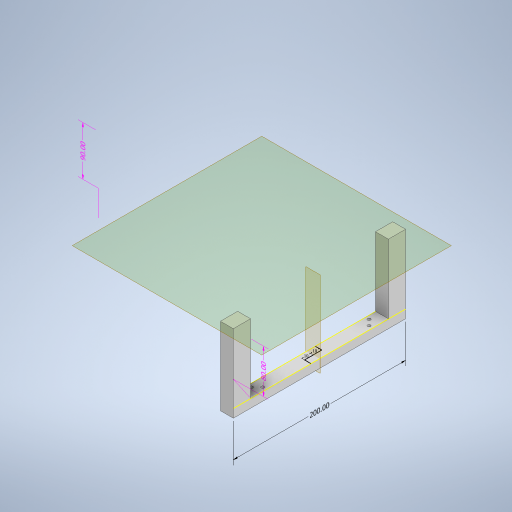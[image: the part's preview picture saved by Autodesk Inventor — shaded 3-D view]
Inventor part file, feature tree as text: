
AUTODESK INVENTOR PART (.ipt)
format: ipt  version: 2023 (Build 270158000, 158)  size: 368,128 bytes
history: native  units: mm
features: sketch x8, other x5, extrude x5, hole x2, plane x2, split x1
ambient origin geometry x8: Origin, YZ Plane, XZ Plane, XY Plane, X Axis, Y Axis, Z Axis, Center Point
bodies: Body1 (feature_tree)
feature tree (23):
  other  "Sólido1"
  other  "Anotaciones"
  extrude  "Extrusión1"  Depth=200.0mm
  hole  "Agujero1"  [1 undecoded]
  extrude  "Extrusión2"  Depth=15.0mm
  extrude  "Extrusión3"  Depth=80.0mm TaperAngle=0.0deg
  extrude  "Extrusión4"  Depth=200.0mm
  extrude  "Extrusión5"  Depth=20.0mm
  hole  "Agujero2"  [1 undecoded]
  plane  "Plano de trabajo1"
  split  "Dividir1"
  plane  "Plano de trabajo2"
  sketch  "Boceto9"  dims[d37=20.0mm d38=20.0mm d39=90.0mm d40=0.0mm d42=10.0mm d43=30.0mm d44=0.0mm d46=1.75mm d47=1.75mm d48=1.75mm d49=1.75mm d50=10.0mm d51=10.0mm d52=15.0mm d56=3.5mm d57=6.0mm d58=4.0mm d59=2.0mm d60=90.0deg d61=8.0mm d62=20.594885mm d63=10.0mm d65=10.0mm d66=10.0mm d67=31.75mm d70=15.0mm d74=200.0mm d78=20.0mm d82=90.0deg d86=10.0mm d87=10.0mm d75=1.454734mm d76=6.982969mm d77=80.0mm d79=4.097996mm d80=1.406125mm d81=90.0mm d83=1.657181mm d84=1.253427mm d85=200.0mm]
  sketch  "Boceto2"  dims[d7=15.0mm d8=200.0mm]
  sketch  "Boceto3"  dims[d9=10.0mm d10=0.0mm]
  sketch  "Boceto4"  dims[d12=1.75mm d13=1.75mm d14=1.75mm d15=1.75mm d16=10.0mm d17=10.0mm d19=30.0mm]
  sketch  "Boceto5"  dims[d20=3.5mm d21=6.0mm d22=4.0mm d23=2.0mm d24=90.0deg d25=8.0mm d26=20.594885mm d27=15.0mm]
  sketch  "Boceto6"  dims[d28=20.0mm d29=80.0mm d30=0.0mm]
  sketch  "Boceto7"  dims[d31=48.0mm d32=200.0mm]
  sketch  "Boceto8"  dims[d33=110.0mm d34=0.0mm d36=20.0mm]
  other  "Cota lineal 2"
  other  "Cota lineal 3"
  other  "Cota lineal 4"
note: 2 required parameter values undecoded (feature->parameter linkage not recoverable at this tier; creation-order binding heuristic only, values carry confidence <= 0.55)
